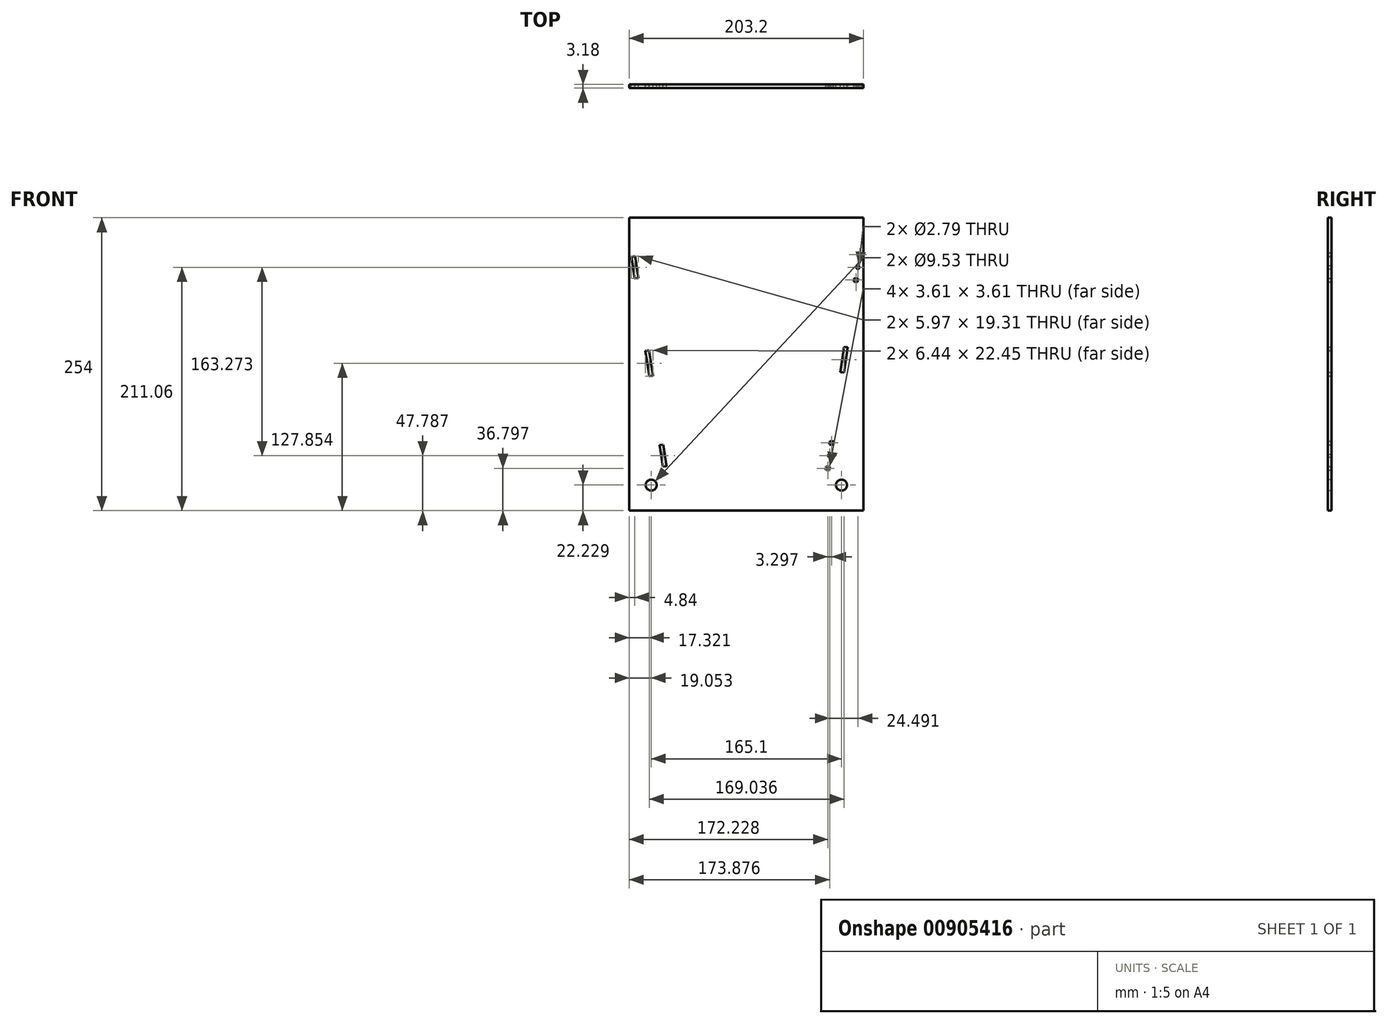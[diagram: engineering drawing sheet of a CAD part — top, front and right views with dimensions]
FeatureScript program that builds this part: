
annotation { "Feature Type Name" : "Feature", "Feature Type Description" : "" }
export const myFeature = defineFeature(function(context is Context, id is Id, definition is map)
    precondition{}
    {
        {
            var Q0;
            Q0=qCreatedBy(makeId("Front.planeOp"),FACE);
            var sketch = newSketch(context, id + "F0", { "sketchPlane" : qUnion([Q0])});
            skLineSegment(sketch, "E0.left", {"start": v(-101.4, 252.7) * mm, "end": v(-101.4, -1.3) * mm});
            skCircle(sketch, "E1", {"center": v(-82.36, 20.92) * mm, "radius": 4.76 * mm});
            skLineSegment(sketch, "E2", {"start": v(-82.36, 20.92) * mm, "end": v(-101.4, 20.92) * mm, "construction": true});
            skLineSegment(sketch, "E3", {"start": v(-82.36, 20.92) * mm, "end": v(-82.36, -1.3) * mm, "construction": true});
            skLineSegment(sketch, "E4", {"start": v(-70.17, 44.46) * mm, "end": v(-73.31, 44) * mm, "construction": true});
            skLineSegment(sketch, "E5", {"start": v(-71.77, 33.68) * mm, "end": v(-75.53, 58.8) * mm});
            skLineSegment(sketch, "E6", {"start": v(-75.53, 58.8) * mm, "end": v(-72.4, 59.27) * mm});
            skLineSegment(sketch, "E7", {"start": v(-71.77, 33.68) * mm, "end": v(-68.63, 34.15) * mm});
            skLineSegment(sketch, "E8", {"start": v(-68.63, 34.15) * mm, "end": v(-72.4, 59.27) * mm});
            skLineSegment(sketch, "E9", {"start": v(-63.3, -1.3) * mm, "end": v(-62.35, -7.66) * mm, "construction": true});
            skLineSegment(sketch, "E10", {"start": v(-62.35, -7.66) * mm, "end": v(-65.56, -7.66) * mm, "construction": true});
            skLineSegment(sketch, "E11", {"start": v(-101.4, 231.3) * mm, "end": v(-98.27, 231.76) * mm});
            skLineSegment(sketch, "E12", {"start": v(-101.4, -1.3) * mm, "end": v(0.2, -1.3) * mm, "construction": true});
            skLineSegment(sketch, "E13", {"start": v(0.2, -1.3) * mm, "end": v(0.2, 252.7) * mm});
            skLineSegment(sketch, "E14", {"start": v(0.2, -1.3) * mm, "end": v(-101.4, -1.3) * mm});
            skLineSegment(sketch, "E15", {"start": v(-101.4, 252.7) * mm, "end": v(0.2, 252.7) * mm});
            skLineSegment(sketch, "E16", {"start": v(-96.88, 222.55) * mm, "end": v(-100.02, 222.07) * mm});
            skLineSegment(sketch, "E17", {"start": v(-100.02, 222.07) * mm, "end": v(-96.26, 196.96) * mm});
            skLineSegment(sketch, "E18", {"start": v(-96.26, 196.96) * mm, "end": v(-93.12, 197.43) * mm});
            skLineSegment(sketch, "E19", {"start": v(-93.12, 197.43) * mm, "end": v(-96.88, 222.55) * mm});
            skLineSegment(sketch, "E20", {"start": v(-63.3, -1.3) * mm, "end": v(-98.27, 231.76) * mm, "construction": true});
            skLineSegment(sketch, "E21", {"start": v(-96.26, 196.96) * mm, "end": v(-85.9, 127.88) * mm, "construction": true});
            skLineSegment(sketch, "E22", {"start": v(-85.9, 127.88) * mm, "end": v(-87.78, 140.44) * mm});
            skLineSegment(sketch, "E23", {"start": v(-87.78, 140.44) * mm, "end": v(-84.64, 140.9) * mm});
            skLineSegment(sketch, "E24", {"start": v(-84.64, 140.9) * mm, "end": v(-80.87, 115.79) * mm});
            skLineSegment(sketch, "E25", {"start": v(-80.87, 115.79) * mm, "end": v(-84.01, 115.32) * mm});
            skLineSegment(sketch, "E26", {"start": v(-84.01, 115.32) * mm, "end": v(-85.9, 127.88) * mm});
            skLineSegment(sketch, "E27", {"start": v(-65.56, -7.66) * mm, "end": v(-101.4, 231.3) * mm, "construction": true});
            skLineSegment(sketch, "E28", {"start": v(-96.88, 222.55) * mm, "end": v(-96.26, 196.96) * mm, "construction": true});
            skLineSegment(sketch, "E29", {"start": v(-84.64, 140.9) * mm, "end": v(-84.01, 115.32) * mm, "construction": true});
            skLineSegment(sketch, "E30", {"start": v(-72.4, 59.27) * mm, "end": v(-71.77, 33.68) * mm, "construction": true});
            skCircle(sketch, "E31", {"center": v(-72.08, 46.48) * mm, "radius": 1.4 * mm});
            skCircle(sketch, "E32", {"center": v(-84.32, 128.11) * mm, "radius": 1.4 * mm});
            skCircle(sketch, "E33", {"center": v(-96.57, 209.75) * mm, "radius": 1.4 * mm});
            skLineSegment(sketch, "E34", {"start": v(-100.02, 222.07) * mm, "end": v(-99.55, 218.93) * mm});
            skLineSegment(sketch, "E35", {"start": v(-99.55, 218.93) * mm, "end": v(-96.41, 219.4) * mm});
            skLineSegment(sketch, "E36", {"start": v(-96.88, 222.55) * mm, "end": v(-96.41, 219.4) * mm});
            skLineSegment(sketch, "E37", {"start": v(-96.26, 196.96) * mm, "end": v(-96.73, 200.1) * mm});
            skLineSegment(sketch, "E38", {"start": v(-96.73, 200.1) * mm, "end": v(-93.59, 200.57) * mm});
            skLineSegment(sketch, "E39", {"start": v(-93.59, 200.57) * mm, "end": v(-93.12, 197.43) * mm});
            skLineSegment(sketch, "E40", {"start": v(-84.01, 115.32) * mm, "end": v(-84.48, 118.46) * mm});
            skLineSegment(sketch, "E41", {"start": v(-84.48, 118.46) * mm, "end": v(-81.34, 118.93) * mm});
            skLineSegment(sketch, "E42", {"start": v(-80.87, 115.79) * mm, "end": v(-81.34, 118.93) * mm});
            skLineSegment(sketch, "E43", {"start": v(-87.78, 140.44) * mm, "end": v(-87.3, 137.3) * mm});
            skLineSegment(sketch, "E44", {"start": v(-87.3, 137.3) * mm, "end": v(-84.17, 137.77) * mm});
            skLineSegment(sketch, "E45", {"start": v(-84.64, 140.9) * mm, "end": v(-84.17, 137.77) * mm});
            skLineSegment(sketch, "E46", {"start": v(-75.53, 58.8) * mm, "end": v(-75.06, 55.66) * mm});
            skLineSegment(sketch, "E47", {"start": v(-75.06, 55.66) * mm, "end": v(-71.92, 56.13) * mm});
            skLineSegment(sketch, "E48", {"start": v(-72.4, 59.27) * mm, "end": v(-71.92, 56.13) * mm});
            skLineSegment(sketch, "E49", {"start": v(-71.77, 33.68) * mm, "end": v(-72.24, 36.82) * mm});
            skLineSegment(sketch, "E50", {"start": v(-72.24, 36.82) * mm, "end": v(-69.1, 37.3) * mm});
            skLineSegment(sketch, "E51", {"start": v(-69.1, 37.3) * mm, "end": v(-68.63, 34.15) * mm});
            skLineSegment(sketch, "E52.MirrorCS", {"start": v(85.03, 140.9) * mm, "end": v(84.55, 137.77) * mm});
            skLineSegment(sketch, "E53.MirrorCS", {"start": v(97.11, 200.1) * mm, "end": v(93.97, 200.57) * mm});
            skLineSegment(sketch, "E54.MirrorCS", {"start": v(75.45, 55.66) * mm, "end": v(72.3, 56.13) * mm});
            skLineSegment(sketch, "E55.MirrorCS", {"start": v(88.17, 140.44) * mm, "end": v(87.7, 137.3) * mm});
            skLineSegment(sketch, "E56.MirrorCS", {"start": v(72.15, 33.68) * mm, "end": v(72.62, 36.82) * mm});
            skLineSegment(sketch, "E57.MirrorCS", {"start": v(93.5, 197.43) * mm, "end": v(97.27, 222.55) * mm});
            skLineSegment(sketch, "E58.MirrorCS", {"start": v(88.17, 140.44) * mm, "end": v(85.03, 140.9) * mm});
            skLineSegment(sketch, "E59.MirrorCS", {"start": v(93.97, 200.57) * mm, "end": v(93.5, 197.43) * mm});
            skLineSegment(sketch, "E60.MirrorCS", {"start": v(96.64, 196.96) * mm, "end": v(97.11, 200.1) * mm});
            skLineSegment(sketch, "E61.MirrorCS", {"start": v(96.64, 196.96) * mm, "end": v(93.5, 197.43) * mm});
            skLineSegment(sketch, "E62.MirrorCS", {"start": v(84.4, 115.32) * mm, "end": v(86.28, 127.88) * mm});
            skLineSegment(sketch, "E63.MirrorCS", {"start": v(84.4, 115.32) * mm, "end": v(84.87, 118.46) * mm});
            skCircle(sketch, "E64.MirrorC", {"center": v(84.71, 128.11) * mm, "radius": 1.4 * mm});
            skLineSegment(sketch, "E65.MirrorCS", {"start": v(97.27, 222.55) * mm, "end": v(96.8, 219.4) * mm});
            skLineSegment(sketch, "E66.MirrorCS", {"start": v(72.78, 59.27) * mm, "end": v(72.3, 56.13) * mm});
            skLineSegment(sketch, "E67.MirrorCS", {"start": v(87.7, 137.3) * mm, "end": v(84.55, 137.77) * mm});
            skLineSegment(sketch, "E68.MirrorCS", {"start": v(72.62, 36.82) * mm, "end": v(69.48, 37.3) * mm});
            skLineSegment(sketch, "E69.MirrorCS", {"start": v(100.41, 222.07) * mm, "end": v(99.94, 218.93) * mm});
            skLineSegment(sketch, "E70.MirrorCS", {"start": v(86.28, 127.88) * mm, "end": v(88.17, 140.44) * mm});
            skLineSegment(sketch, "E71.MirrorCS", {"start": v(69.01, 34.15) * mm, "end": v(72.78, 59.27) * mm});
            skCircle(sketch, "E72.MirrorC", {"center": v(96.96, 209.75) * mm, "radius": 1.4 * mm});
            skLineSegment(sketch, "E73.MirrorCS", {"start": v(97.27, 222.55) * mm, "end": v(96.64, 196.96) * mm, "construction": true});
            skLineSegment(sketch, "E74.MirrorCS", {"start": v(85.03, 140.9) * mm, "end": v(81.26, 115.79) * mm});
            skLineSegment(sketch, "E75.MirrorCS", {"start": v(72.78, 59.27) * mm, "end": v(72.15, 33.68) * mm, "construction": true});
            skLineSegment(sketch, "E76.MirrorCS", {"start": v(100.41, 222.07) * mm, "end": v(96.64, 196.96) * mm});
            skLineSegment(sketch, "E77.MirrorCS", {"start": v(97.27, 222.55) * mm, "end": v(100.41, 222.07) * mm});
            skLineSegment(sketch, "E78.MirrorCS", {"start": v(85.03, 140.9) * mm, "end": v(84.4, 115.32) * mm, "construction": true});
            skLineSegment(sketch, "E79.MirrorCS", {"start": v(75.92, 58.8) * mm, "end": v(75.45, 55.66) * mm});
            skLineSegment(sketch, "E80.MirrorCS", {"start": v(70.56, 44.46) * mm, "end": v(73.7, 44) * mm, "construction": true});
            skLineSegment(sketch, "E81.MirrorCS", {"start": v(72.15, 33.68) * mm, "end": v(75.92, 58.8) * mm});
            skLineSegment(sketch, "E82.MirrorCS", {"start": v(75.92, 58.8) * mm, "end": v(72.78, 59.27) * mm});
            skLineSegment(sketch, "E83.MirrorCS", {"start": v(81.26, 115.79) * mm, "end": v(81.73, 118.93) * mm});
            skLineSegment(sketch, "E84.MirrorCS", {"start": v(84.87, 118.46) * mm, "end": v(81.73, 118.93) * mm});
            skLineSegment(sketch, "E85.MirrorCS", {"start": v(72.15, 33.68) * mm, "end": v(69.01, 34.15) * mm});
            skLineSegment(sketch, "E86.MirrorCS", {"start": v(69.48, 37.3) * mm, "end": v(69.01, 34.15) * mm});
            skLineSegment(sketch, "E87.MirrorCS", {"start": v(99.94, 218.93) * mm, "end": v(96.8, 219.4) * mm});
            skCircle(sketch, "E88.MirrorC", {"center": v(72.47, 46.48) * mm, "radius": 1.4 * mm});
            skLineSegment(sketch, "E89.MirrorCS", {"start": v(101.8, 231.3) * mm, "end": v(98.65, 231.76) * mm});
            skLineSegment(sketch, "E90.MirrorCS", {"start": v(81.26, 115.79) * mm, "end": v(84.4, 115.32) * mm});
            skCircle(sketch, "E91.MirrorC", {"center": v(82.74, 20.92) * mm, "radius": 4.76 * mm});
            skLineSegment(sketch, "E92.MirrorCS", {"start": v(63.7, -1.3) * mm, "end": v(62.74, -7.66) * mm, "construction": true});
            skLineSegment(sketch, "E93.MirrorCS", {"start": v(62.74, -7.66) * mm, "end": v(65.95, -7.66) * mm, "construction": true});
            skLineSegment(sketch, "E94.MirrorCS", {"start": v(82.74, 20.92) * mm, "end": v(101.8, 20.92) * mm, "construction": true});
            skLineSegment(sketch, "E95.MirrorCS", {"start": v(82.74, 20.92) * mm, "end": v(82.74, -1.3) * mm, "construction": true});
            skLineSegment(sketch, "E96.MirrorCS", {"start": v(96.64, 196.96) * mm, "end": v(86.28, 127.88) * mm, "construction": true});
            skLineSegment(sketch, "E97.MirrorCS", {"start": v(0.2, -1.3) * mm, "end": v(101.8, -1.3) * mm});
            skLineSegment(sketch, "E98.MirrorCS", {"start": v(101.8, 252.7) * mm, "end": v(0.2, 252.7) * mm});
            skLineSegment(sketch, "E99.MirrorCS", {"start": v(65.95, -7.66) * mm, "end": v(101.8, 231.3) * mm, "construction": true});
            skLineSegment(sketch, "E100.MirrorCS", {"start": v(101.8, 252.7) * mm, "end": v(101.8, -1.3) * mm});
            skLineSegment(sketch, "E101.MirrorCS", {"start": v(101.8, -1.3) * mm, "end": v(0.2, -1.3) * mm, "construction": true});
            skLineSegment(sketch, "E102.MirrorCS", {"start": v(63.7, -1.3) * mm, "end": v(98.65, 231.76) * mm, "construction": true});
            skSolve(sketch);
        }
        {
            var Q0;
            Q0=makeQuery(id+"F0.imprint","IMPRINT",FACE,{"disambiguationData":[TD([[makeQuery(id+"F0.imprint","IMPRINT",EDGE,{"derivedFrom":sQuery(id+"F0.wireOp",EDGE,"E1")}),-1.0]])]});
            var Q1;
            Q1=makeQuery(id+"F0.imprint","IMPRINT",FACE,{"disambiguationData":[TD([[makeQuery(id+"F0.imprint","IMPRINT",EDGE,{"derivedFrom":sQuery(id+"F0.wireOp",EDGE,"E13")}),-1.0]])]});
            var Q2;
            Q2=makeQuery(id+"F0.imprint","IMPRINT",FACE,{"disambiguationData":[TD([[makeQuery(id+"F0.imprint","IMPRINT",EDGE,{"derivedFrom":sQuery(id+"F0.wireOp",EDGE,"E22")}),-1.0]])]});
            var Q3;
            Q3=makeQuery(id+"F0.imprint","IMPRINT",FACE,{"disambiguationData":[TD([[makeQuery(id+"F0.imprint","IMPRINT",EDGE,{"derivedFrom":sQuery(id+"F0.wireOp",EDGE,"E17")}),1.0]])]});
            var Q4;
            Q4=makeQuery(id+"F0.imprint","IMPRINT",FACE,{"disambiguationData":[TD([[makeQuery(id+"F0.imprint","IMPRINT",EDGE,{"derivedFrom":sQuery(id+"F0.wireOp",EDGE,"E5")}),-1.0]])]});
            var Q5;
            {var subQ1=sQuery(id+"F0.wireOp",EDGE,"E54.MirrorCS");Q5=makeQuery(id+"F0.imprint","IMPRINT",FACE,{"disambiguationData":[TD([[makeQuery(id+"F0.imprint","IMPRINT",EDGE,{"derivedFrom":subQ1}),1.0]])]});}
            var Q6;
            {var subQ1=sQuery(id+"F0.wireOp",EDGE,"E62.MirrorCS");Q6=makeQuery(id+"F0.imprint","IMPRINT",FACE,{"disambiguationData":[TD([[makeQuery(id+"F0.imprint","IMPRINT",EDGE,{"derivedFrom":subQ1}),1.0]])]});}
            var Q7;
            {var subQ1=sQuery(id+"F0.wireOp",EDGE,"E53.MirrorCS");Q7=makeQuery(id+"F0.imprint","IMPRINT",FACE,{"disambiguationData":[TD([[makeQuery(id+"F0.imprint","IMPRINT",EDGE,{"derivedFrom":subQ1}),-1.0]])]});}
            extrude(context, id + "F1", {"entities" : qUnion([Q0, Q1, Q2, Q3, Q4, Q5, Q6, Q7]), "depth" : 3.17 * mm, "offsetDistance" : 25.4 * mm});
        }
    });
